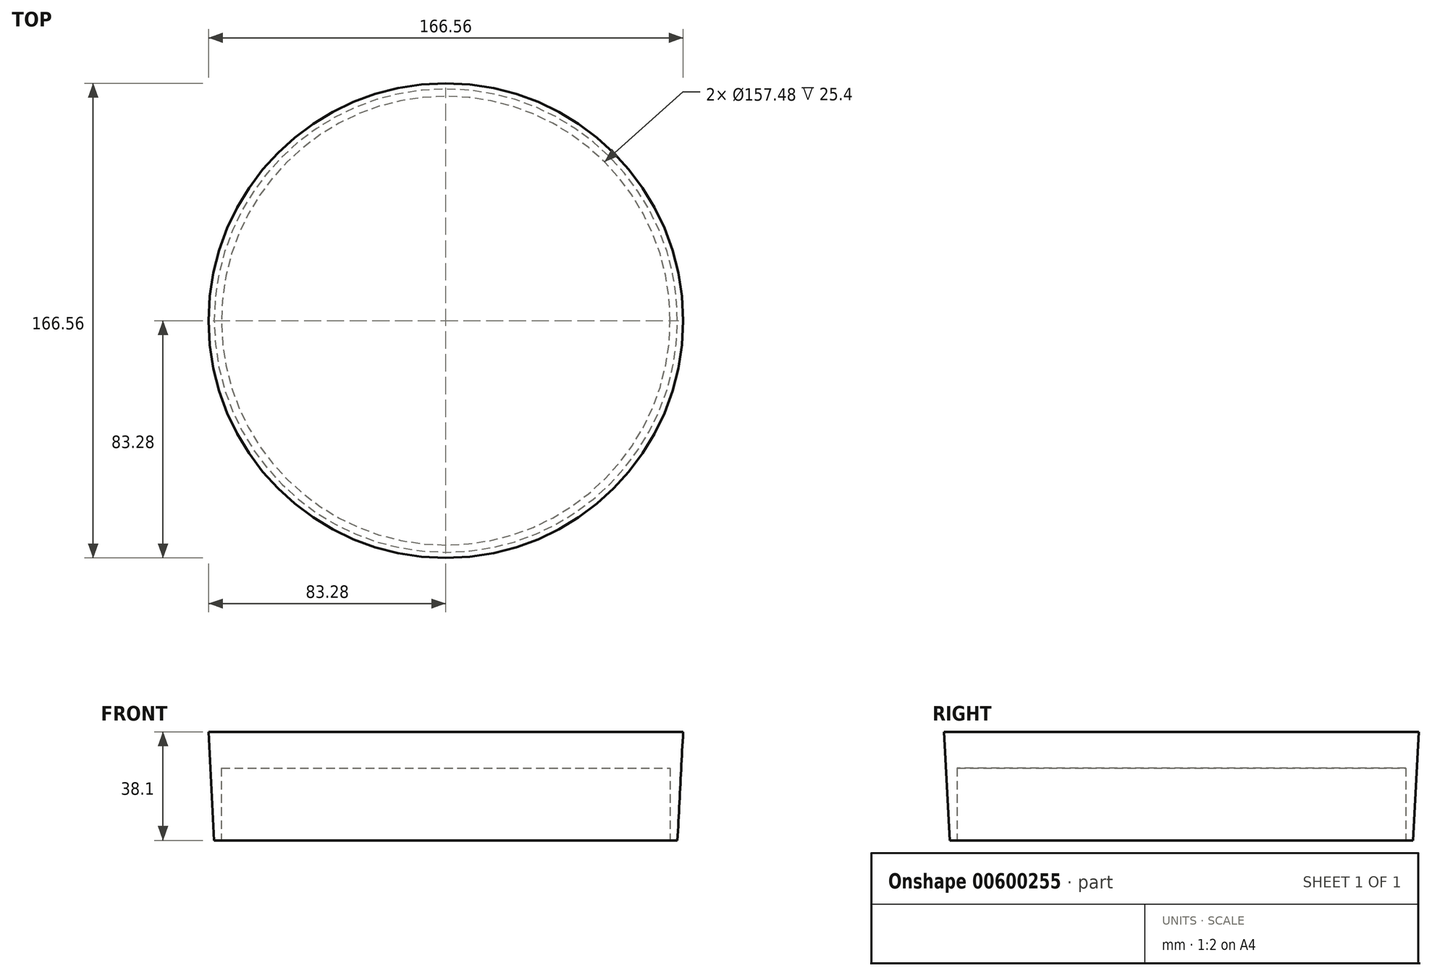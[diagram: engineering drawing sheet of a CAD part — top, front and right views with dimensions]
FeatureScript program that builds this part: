
annotation { "Feature Type Name" : "Feature", "Feature Type Description" : "" }
export const myFeature = defineFeature(function(context is Context, id is Id, definition is map)
    precondition{}
    {
        {
            var Q0;
            Q0=qCreatedBy(makeId("Top.planeOp"),FACE);
            var sketch = newSketch(context, id + "F0", { "sketchPlane" : qUnion([Q0])});
            skCircle(sketch, "E0", {"center": v(0, 0) * mm, "radius": 81.28 * mm});
            skSolve(sketch);
        }
        {
            var Q0;
            Q0=makeQuery(id+"F0.imprint","IMPRINT",FACE,{"disambiguationData":[TD([[makeQuery(id+"F0.imprint","IMPRINT",EDGE,{"derivedFrom":sQuery(id+"F0.wireOp",EDGE,"E0")}),1.0]])]});
            extrude(context, id + "F1", {"entities" : qUnion([Q0]), "depth" : 38.1 * mm, "offsetDistance" : 25.4 * mm, "hasDraft" : true, "draftAngle" : 3 * degree});
        }
        {
            var Q0;
            Q0=makeQuery(id+"F1.opExtrude","CAP_FACE",FACE,{"disambiguationData":[OSD([sQuery(id+"F0.wireOp",EDGE,"E0")])],"isStart":true});
            var sketch = newSketch(context, id + "F2", { "sketchPlane" : qUnion([Q0])});
            skCircle(sketch, "E1", {"center": v(0, 0) * mm, "radius": 78.74 * mm});
            skSolve(sketch);
        }
        {
            var Q0;
            Q0=makeQuery(id+"F2.imprint","IMPRINT",FACE,{"disambiguationData":[TD([[makeQuery(id+"F2.imprint","IMPRINT",EDGE,{"derivedFrom":sQuery(id+"F2.wireOp",EDGE,"E1")}),1.0]])]});
            extrude(context, id + "F3", {"entities" : qUnion([Q0]), "operationType" : NewBodyOperationType.REMOVE, "oppositeDirection" : true, "depth" : 25.4 * mm, "offsetDistance" : 25.4 * mm});
        }
    });
